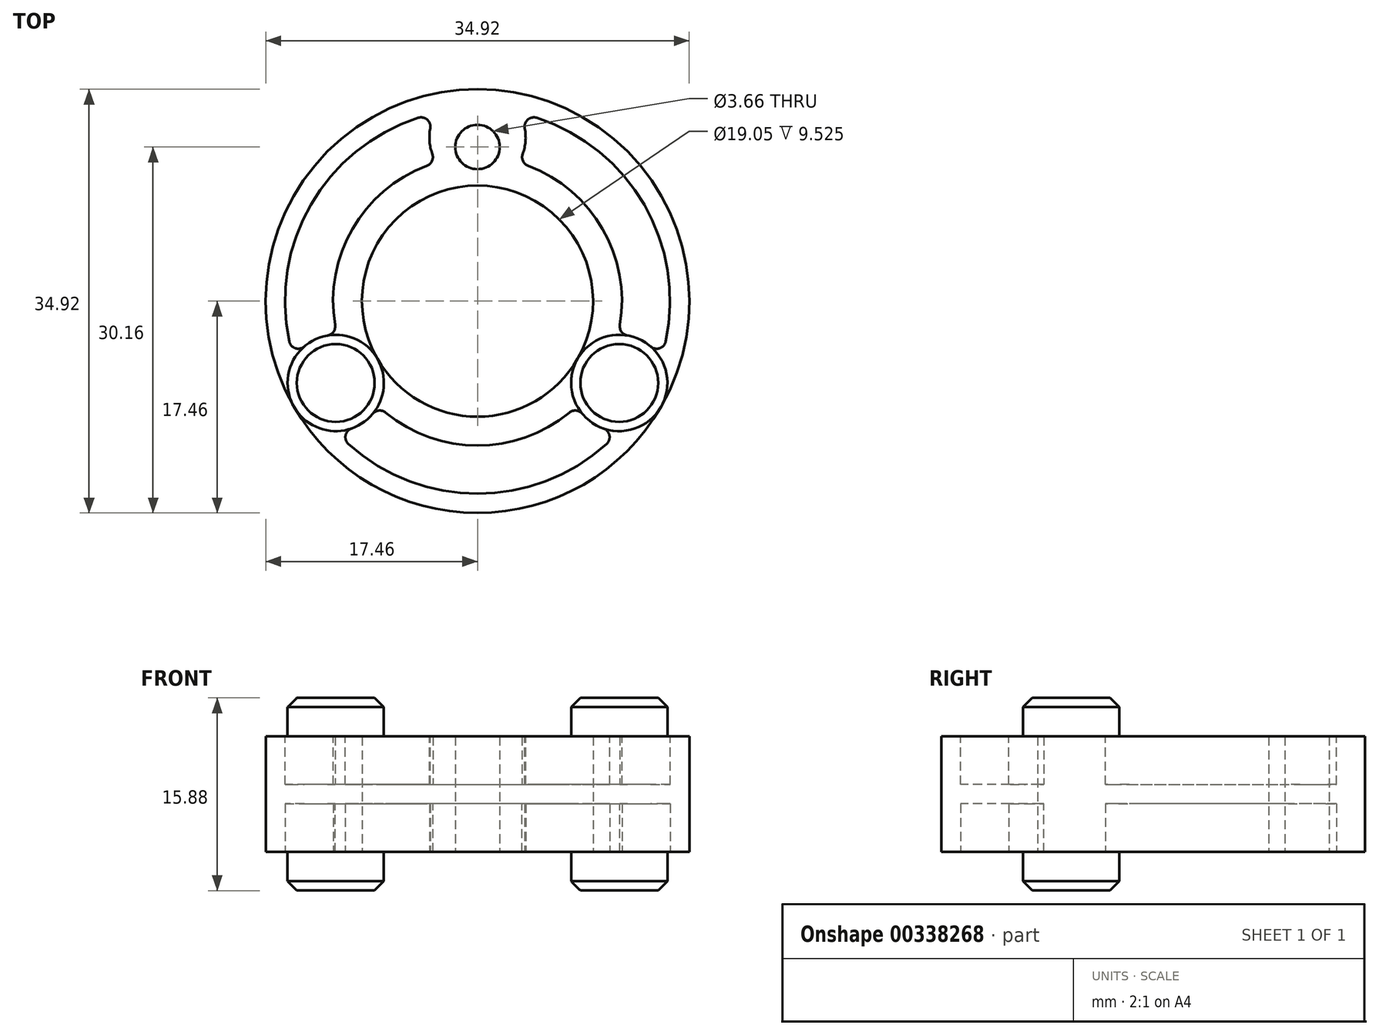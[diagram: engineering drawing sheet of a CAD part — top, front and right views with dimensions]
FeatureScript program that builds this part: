
annotation { "Feature Type Name" : "Feature", "Feature Type Description" : "" }
export const myFeature = defineFeature(function(context is Context, id is Id, definition is map)
    precondition{}
    {
        {
            var Q0;
            Q0=qCreatedBy(makeId("Top.planeOp"),FACE);
            var sketch = newSketch(context, id + "F0", { "sketchPlane" : qUnion([Q0])});
            skCircle(sketch, "E0", {"center": v(0, 0) * mm, "radius": 9.53 * mm});
            skCircle(sketch, "E1", {"center": v(0, 0) * mm, "radius": 17.46 * mm});
            skLineSegment(sketch, "E2", {"start": v(0, 0) * mm, "end": v(0, 12.7) * mm, "construction": true});
            skCircle(sketch, "E3", {"center": v(0, 12.7) * mm, "radius": 1.83 * mm});
            skSolve(sketch);
        }
        {
            var Q0;
            Q0=qSketchRegion(id+"F0",true);
            extrude(context, id + "F1", {"entities" : qUnion([Q0]), "depth" : 9.52 * mm});
        }
        {
            var Q0;
            {var subQ0=sQuery(id+"F0.wireOp",EDGE,"E1");var subQ1=makeQuery(id+"F1.opExtrude","CAP_FACE",FACE,{"disambiguationData":[OSD([sQuery(id+"F0.wireOp",EDGE,"E0"),subQ0,sQuery(id+"F0.wireOp",EDGE,"E3")])],"isStart":false});Q0=makeQuery(id+"FaGNQa3NOKQJJ3d_1.boolean.opBoolean","SPLIT",FACE,{"disambiguationData":[TD([subQ1,makeQuery(id+"F1.opExtrude","SWEPT_FACE",FACE,{"disambiguationData":[OSD([subQ0])]}),makeQuery(id+"FBX2u8IMGBDlIgd_1.boolean.opBoolean","COPY",FACE,{"derivedFrom":makeQuery(id+"FBX2u8IMGBDlIgd_1.opExtrude","SWEPT_FACE",FACE,{"disambiguationData":[OSD([sQuery(id+"F7rsySl2JD6qCkH_1.wireOp",EDGE,"BS3xaHe7-TctR-HWj4-VqEs-X0m0ugFKdukP")])]})}),makeQuery(id+"FaGNQa3NOKQJJ3d_1.opExtrude","SWEPT_FACE",FACE,{"disambiguationData":[OSD([sQuery(id+"FimIUrEkqtjUp3z_1.wireOp",EDGE,"HlGXKecl-ggte-uXjZ-GF2z-oe2yHpBcJ9Dq")])]}),makeQuery(id+"FaGNQa3NOKQJJ3d_1.opExtrude","SWEPT_FACE",FACE,{"disambiguationData":[OSD([sQuery(id+"FimIUrEkqtjUp3z_1.wireOp",EDGE,"b06J7RxP-un1X-OzPm-o8VI-wkIMPVGFyDBE")])]})])],"derivedFrom":subQ1});}
            var sketch = newSketch(context, id + "F2", { "sketchPlane" : qUnion([Q0])});
            skArc(sketch, "E4", {"start": v(-3.42, 15.5) * mm, "mid": v(-3.97, 13.45) * mm, "end": v(-3.38, 11.42) * mm});
            skArc(sketch, "E5", {"start": v(-3.38, 11.42) * mm, "mid": v(-10.31, 5.95) * mm, "end": v(-11.58, -2.78) * mm});
            skArc(sketch, "E6", {"start": v(-3.42, 15.5) * mm, "mid": v(-13.75, 7.94) * mm, "end": v(-15.14, -4.79) * mm});
            skLineSegment(sketch, "E7", {"start": v(0, 0) * mm, "end": v(0, 13.5) * mm, "construction": true});
            skArc(sketch, "E8", {"start": v(-11.58, -2.78) * mm, "mid": v(-13.63, -3.29) * mm, "end": v(-15.14, -4.79) * mm});
            skArc(sketch, "E9", {"start": v(-15.14, -4.79) * mm, "mid": v(-9.74, -10.2) * mm, "end": v(-11.58, -2.78) * mm, "construction": true});
            skLineSegment(sketch, "E10", {"start": v(-11.69, -6.75) * mm, "end": v(0, 0) * mm, "construction": true});
            skSolve(sketch);
        }
        {
            var Q0;
            Q0=qSketchRegion(id+"F2",true);
            extrude(context, id + "F3", {"entities" : qUnion([Q0]), "operationType" : NewBodyOperationType.REMOVE, "oppositeDirection" : true, "depth" : 3.97 * mm});
        }
        {
            var Q0;
            Q0=makeQuery(id+"F1.opExtrude","CAP_FACE",FACE,{"disambiguationData":[OSD([sQuery(id+"F0.wireOp",EDGE,"E0"),sQuery(id+"F0.wireOp",EDGE,"E1"),sQuery(id+"F0.wireOp",EDGE,"E3")])],"isStart":true});
            var sketch = newSketch(context, id + "F4", { "sketchPlane" : qUnion([Q0])});
            skArc(sketch, "E11", {"start": v(-15.14, 4.79) * mm, "mid": v(-13.75, -7.94) * mm, "end": v(-3.42, -15.5) * mm});
            skArc(sketch, "E12", {"start": v(-11.58, 2.78) * mm, "mid": v(-10.31, -5.95) * mm, "end": v(-3.38, -11.42) * mm});
            skArc(sketch, "E13", {"start": v(-15.14, 4.79) * mm, "mid": v(-13.63, 3.29) * mm, "end": v(-11.58, 2.78) * mm});
            skArc(sketch, "E14", {"start": v(-3.38, -11.42) * mm, "mid": v(-3.97, -13.45) * mm, "end": v(-3.42, -15.5) * mm});
            skSolve(sketch);
        }
        {
            var Q0;
            Q0=qSketchRegion(id+"F4",true);
            extrude(context, id + "F5", {"entities" : qUnion([Q0]), "operationType" : NewBodyOperationType.REMOVE, "oppositeDirection" : true, "depth" : 3.97 * mm});
        }
        {
            var Q0;
            Q0=makeQuery(id+"F3.boolean.opBoolean","COPY",EDGE,{"derivedFrom":makeQuery(id+"F3.opExtrude","SWEPT_EDGE",EDGE,{"disambiguationData":[OSD([sQuery(id+"F2.wireOp",EDGE,"E6"),sQuery(id+"F2.wireOp",EDGE,"E8")])]})});
            var Q1;
            Q1=makeQuery(id+"F3.boolean.opBoolean","COPY",EDGE,{"derivedFrom":makeQuery(id+"F3.opExtrude","SWEPT_EDGE",EDGE,{"disambiguationData":[OSD([sQuery(id+"F2.wireOp",EDGE,"E5"),sQuery(id+"F2.wireOp",EDGE,"E8")])]})});
            var Q2;
            Q2=makeQuery(id+"F3.boolean.opBoolean","COPY",EDGE,{"derivedFrom":makeQuery(id+"F3.opExtrude","SWEPT_EDGE",EDGE,{"disambiguationData":[OSD([sQuery(id+"F2.wireOp",EDGE,"E4"),sQuery(id+"F2.wireOp",EDGE,"E5")])]})});
            var Q3;
            Q3=makeQuery(id+"F3.boolean.opBoolean","COPY",EDGE,{"derivedFrom":makeQuery(id+"F3.opExtrude","SWEPT_EDGE",EDGE,{"disambiguationData":[OSD([sQuery(id+"F2.wireOp",EDGE,"E4"),sQuery(id+"F2.wireOp",EDGE,"E6")])]})});
            var Q4;
            Q4=makeQuery(id+"F5.boolean.opBoolean","COPY",EDGE,{"derivedFrom":makeQuery(id+"F5.opExtrude","SWEPT_EDGE",EDGE,{"disambiguationData":[OSD([sQuery(id+"F4.wireOp",EDGE,"E12"),sQuery(id+"F4.wireOp",EDGE,"E14")])]})});
            var Q5;
            Q5=makeQuery(id+"F5.boolean.opBoolean","COPY",EDGE,{"derivedFrom":makeQuery(id+"F5.opExtrude","SWEPT_EDGE",EDGE,{"disambiguationData":[OSD([sQuery(id+"F4.wireOp",EDGE,"E11"),sQuery(id+"F4.wireOp",EDGE,"E14")])]})});
            var Q6;
            Q6=makeQuery(id+"F5.boolean.opBoolean","COPY",EDGE,{"derivedFrom":makeQuery(id+"F5.opExtrude","SWEPT_EDGE",EDGE,{"disambiguationData":[OSD([sQuery(id+"F4.wireOp",EDGE,"E12"),sQuery(id+"F4.wireOp",EDGE,"E13")])]})});
            var Q7;
            Q7=makeQuery(id+"F5.boolean.opBoolean","COPY",EDGE,{"derivedFrom":makeQuery(id+"F5.opExtrude","SWEPT_EDGE",EDGE,{"disambiguationData":[OSD([sQuery(id+"F4.wireOp",EDGE,"E11"),sQuery(id+"F4.wireOp",EDGE,"E13")])]})});
            fillet(context, id + "F6", {"entities" : qUnion([Q0, Q1, Q2, Q3, Q4, Q5, Q6, Q7]), "radius" : 0.76 * mm, "tangentPropagation" : true, "allowEdgeOverflow" : false});
        }
        {
            var Q0;
            Q0=makeQuery(id+"F6.opFillet","BLEND_FACE",FACE,{"disambiguationData":[OSD([sQuery(id+"F2.wireOp",EDGE,"E6"),sQuery(id+"F2.wireOp",EDGE,"E8")])]});
            var Q1;
            Q1=makeQuery(id+"F3.boolean.opBoolean","COPY",FACE,{"derivedFrom":makeQuery(id+"F3.opExtrude","SWEPT_FACE",FACE,{"disambiguationData":[OSD([sQuery(id+"F2.wireOp",EDGE,"E8")])]})});
            var Q2;
            Q2=makeQuery(id+"F6.opFillet","BLEND_FACE",FACE,{"disambiguationData":[OSD([sQuery(id+"F2.wireOp",EDGE,"E5"),sQuery(id+"F2.wireOp",EDGE,"E8")])]});
            var Q3;
            Q3=makeQuery(id+"F3.boolean.opBoolean","COPY",FACE,{"derivedFrom":makeQuery(id+"F3.opExtrude","SWEPT_FACE",FACE,{"disambiguationData":[OSD([sQuery(id+"F2.wireOp",EDGE,"E5")])]})});
            var Q4;
            Q4=makeQuery(id+"F6.opFillet","BLEND_FACE",FACE,{"disambiguationData":[OSD([sQuery(id+"F2.wireOp",EDGE,"E4"),sQuery(id+"F2.wireOp",EDGE,"E5")])]});
            var Q5;
            Q5=makeQuery(id+"F3.boolean.opBoolean","COPY",FACE,{"derivedFrom":makeQuery(id+"F3.opExtrude","SWEPT_FACE",FACE,{"disambiguationData":[OSD([sQuery(id+"F2.wireOp",EDGE,"E4")])]})});
            var Q6;
            Q6=makeQuery(id+"F6.opFillet","BLEND_FACE",FACE,{"disambiguationData":[OSD([sQuery(id+"F2.wireOp",EDGE,"E4"),sQuery(id+"F2.wireOp",EDGE,"E6")])]});
            var Q7;
            Q7=makeQuery(id+"F3.boolean.opBoolean","COPY",FACE,{"derivedFrom":makeQuery(id+"F3.opExtrude","SWEPT_FACE",FACE,{"disambiguationData":[OSD([sQuery(id+"F2.wireOp",EDGE,"E6")])]})});
            var Q8;
            Q8=makeQuery(id+"F6.opFillet","BLEND_FACE",FACE,{"disambiguationData":[OSD([sQuery(id+"F4.wireOp",EDGE,"E11"),sQuery(id+"F4.wireOp",EDGE,"E13")])]});
            var Q9;
            Q9=makeQuery(id+"F5.boolean.opBoolean","COPY",FACE,{"derivedFrom":makeQuery(id+"F5.opExtrude","SWEPT_FACE",FACE,{"disambiguationData":[OSD([sQuery(id+"F4.wireOp",EDGE,"E13")])]})});
            var Q10;
            Q10=makeQuery(id+"F6.opFillet","BLEND_FACE",FACE,{"disambiguationData":[OSD([sQuery(id+"F4.wireOp",EDGE,"E12"),sQuery(id+"F4.wireOp",EDGE,"E13")])]});
            var Q11;
            Q11=makeQuery(id+"F5.boolean.opBoolean","COPY",FACE,{"derivedFrom":makeQuery(id+"F5.opExtrude","SWEPT_FACE",FACE,{"disambiguationData":[OSD([sQuery(id+"F4.wireOp",EDGE,"E12")])]})});
            var Q12;
            Q12=makeQuery(id+"F6.opFillet","BLEND_FACE",FACE,{"disambiguationData":[OSD([sQuery(id+"F4.wireOp",EDGE,"E12"),sQuery(id+"F4.wireOp",EDGE,"E14")])]});
            var Q13;
            Q13=makeQuery(id+"F5.boolean.opBoolean","COPY",FACE,{"derivedFrom":makeQuery(id+"F5.opExtrude","SWEPT_FACE",FACE,{"disambiguationData":[OSD([sQuery(id+"F4.wireOp",EDGE,"E14")])]})});
            var Q14;
            Q14=makeQuery(id+"F6.opFillet","BLEND_FACE",FACE,{"disambiguationData":[OSD([sQuery(id+"F4.wireOp",EDGE,"E11"),sQuery(id+"F4.wireOp",EDGE,"E14")])]});
            var Q15;
            Q15=makeQuery(id+"F5.boolean.opBoolean","COPY",FACE,{"derivedFrom":makeQuery(id+"F5.opExtrude","SWEPT_FACE",FACE,{"disambiguationData":[OSD([sQuery(id+"F4.wireOp",EDGE,"E11")])]})});
            var Q16;
            Q16=makeQuery(id+"F3.boolean.opBoolean","COPY",FACE,{"derivedFrom":makeQuery(id+"F3.opExtrude","CAP_FACE",FACE,{"disambiguationData":[OSD([sQuery(id+"F2.wireOp",EDGE,"E4"),sQuery(id+"F2.wireOp",EDGE,"E5"),sQuery(id+"F2.wireOp",EDGE,"E6"),sQuery(id+"F2.wireOp",EDGE,"E8")])],"isStart":false})});
            var Q17;
            Q17=makeQuery(id+"F5.boolean.opBoolean","COPY",FACE,{"derivedFrom":makeQuery(id+"F5.opExtrude","CAP_FACE",FACE,{"disambiguationData":[OSD([sQuery(id+"F4.wireOp",EDGE,"E11"),sQuery(id+"F4.wireOp",EDGE,"E12"),sQuery(id+"F4.wireOp",EDGE,"E13"),sQuery(id+"F4.wireOp",EDGE,"E14")])],"isStart":false})});
            var Q18;
            Q18=makeQuery(id+"F1.opExtrude","SWEPT_FACE",FACE,{"disambiguationData":[OSD([sQuery(id+"F0.wireOp",EDGE,"E0")])]});
            circularPattern(context, id + "F7", {"patternType" : PatternType.FACE, "faces" : qUnion([Q0, Q1, Q2, Q3, Q4, Q5, Q6, Q7, Q8, Q9, Q10, Q11, Q12, Q13, Q14, Q15, Q16, Q17]), "axis" : qUnion([Q18]), "angle" : 360 * degree, "instanceCount" : 3, "equalSpace" : true});
        }
        {
            var Q0;
            Q0=makeQuery(id+"F1.opExtrude","CAP_FACE",FACE,{"disambiguationData":[OSD([sQuery(id+"F0.wireOp",EDGE,"E0"),sQuery(id+"F0.wireOp",EDGE,"E1"),sQuery(id+"F0.wireOp",EDGE,"E3")])],"isStart":true});
            var sketch = newSketch(context, id + "F8", { "sketchPlane" : qUnion([Q0])});
            skCircle(sketch, "E15", {"center": v(11.69, 6.75) * mm, "radius": 3.97 * mm});
            skCircle(sketch, "E16", {"center": v(-11.69, 6.75) * mm, "radius": 3.97 * mm});
            skSolve(sketch);
        }
        {
            var Q0;
            Q0=qSketchRegion(id+"F8",true);
            extrude(context, id + "F9", {"entities" : qUnion([Q0]), "operationType" : NewBodyOperationType.ADD, "depth" : 3.17 * mm, "hasSecondDirection" : true, "secondDirectionOppositeDirection" : true, "secondDirectionDepth" : 12.7 * mm});
        }
        {
            var Q0;
            Q0=makeQuery(id+"F9.opExtrude","CAP_EDGE",EDGE,{"disambiguationData":[OSD([sQuery(id+"F8.wireOp",EDGE,"E16")])],"isStart":true});
            var Q1;
            Q1=makeQuery(id+"F9.opExtrude","CAP_EDGE",EDGE,{"disambiguationData":[OSD([sQuery(id+"F8.wireOp",EDGE,"E15")])],"isStart":true});
            var Q2;
            Q2=makeQuery(id+"F9.opExtrude","CAP_EDGE",EDGE,{"disambiguationData":[OSD([sQuery(id+"F8.wireOp",EDGE,"E15")])],"isStart":false});
            var Q3;
            Q3=makeQuery(id+"F9.opExtrude","CAP_EDGE",EDGE,{"disambiguationData":[OSD([sQuery(id+"F8.wireOp",EDGE,"E16")])],"isStart":false});
            chamfer(context, id + "F10", {"entities" : qUnion([Q0, Q1, Q2, Q3]), "width" : 0.76 * mm, "tangentPropagation" : true});
        }
    });
